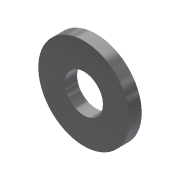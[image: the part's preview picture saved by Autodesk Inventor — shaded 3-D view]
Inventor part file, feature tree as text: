
AUTODESK INVENTOR PART (.ipt)
format: ipt  version: 2013 (Build 170138000, 138)  size: 77,312 bytes
history: native  units: in
note: dims shown in document units (in); Inventor stores cm internally (conversion verified against a paired STEP export)
features: extrude x1, sketch x1
ambient origin geometry x8: Origin, YZ Plane, XZ Plane, XY Plane, X Axis, Y Axis, Z Axis, Center Point
bodies: Solid1 (feature_tree)
feature tree (2):
  extrude  "Extrusion1"  Depth=0.1562in
  sketch  "Sketch1"  dims[d0=0.375in d1=0.1562in d2=0.05in d3=0.0in]
